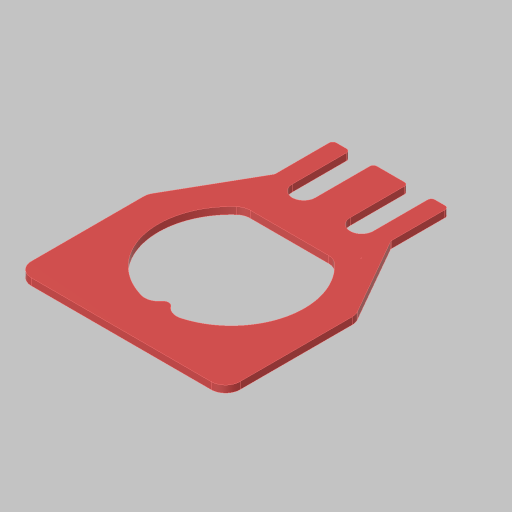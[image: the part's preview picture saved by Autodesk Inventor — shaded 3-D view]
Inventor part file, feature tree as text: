
AUTODESK INVENTOR PART (.ipt)
format: ipt  version: 2023.5 (Build 275446000, 446)  size: 293,376 bytes
history: native  units: in
note: dims shown in document units (in); Inventor stores cm internally (conversion verified against a paired STEP export)
features: sketch x6, extrude x6, fillet x5, projected_geometry x5
ambient origin geometry x8: Origin, YZ Plane, XZ Plane, XY Plane, X Axis, Y Axis, Z Axis, Center Point
bodies: Solid1 (feature_tree)
feature tree (22):
  sketch  "Sketch1"  dims[d1=0.7in d3=0.125in d4=0.197in]
  extrude  "Extrusion1"  Depth=0.125in
  fillet  "Fillet1"  Radius=0.197in
  extrude  "Extrusion2"  Depth=1.0in
  extrude  "Extrusion3"  Depth=0.5in
  fillet  "Fillet2"  Radius=0.5in
  extrude  "Extrusion4"  Depth=0.06in TaperAngle=0.0deg
  fillet  "Fillet3"  Radius=0.125in
  extrude  "Extrusion5"  Depth=0.5in
  fillet  "Fillet4"  Radius=1.375in
  extrude  "Extrusion6"  Depth=1.0in TaperAngle=0.0deg
  fillet  "Fillet5"  Radius=1.26in
  sketch  "Sketch2"  dims[d5=0.197in d8=1.0in]
  sketch  "Sketch3"  dims[d9=2.0in d10=0.25in d11=0.5in]
  sketch  "Sketch4"  dims[d12=0.25in d13=0.06in d14=0.0in d22=0.125in]
  sketch  "Sketch5"  dims[d23=0.201in d24=0.5in d26=1.375in]
  sketch  "Sketch6"  dims[d27=0.5in d28=1.0in d29=0.0in d30=1.26in d31=0.5in d32=0.125in d33=1.0in d34=0.0in d35=0.125in d36=0.093in d37=0.042in d38=1.0in d39=0.0in d40=0.125in d41=0.7874in d43=0.197in d44=0.3937in d46=1.0in d48=1.8in d49=3.45in d50=1.125in d51=1.0in d52=0.0in d53=0.125in d54=1.25in d55=1.0in d57=0.0in d58=0.0in d59=0.0312in]
  projected_geometry  "Project Cut Edges1"
  projected_geometry  "Project Cut Edges2"
  projected_geometry  "Project Cut Edges3"
  projected_geometry  "Project Cut Edges4"
  projected_geometry  "Project Cut Edges5"
